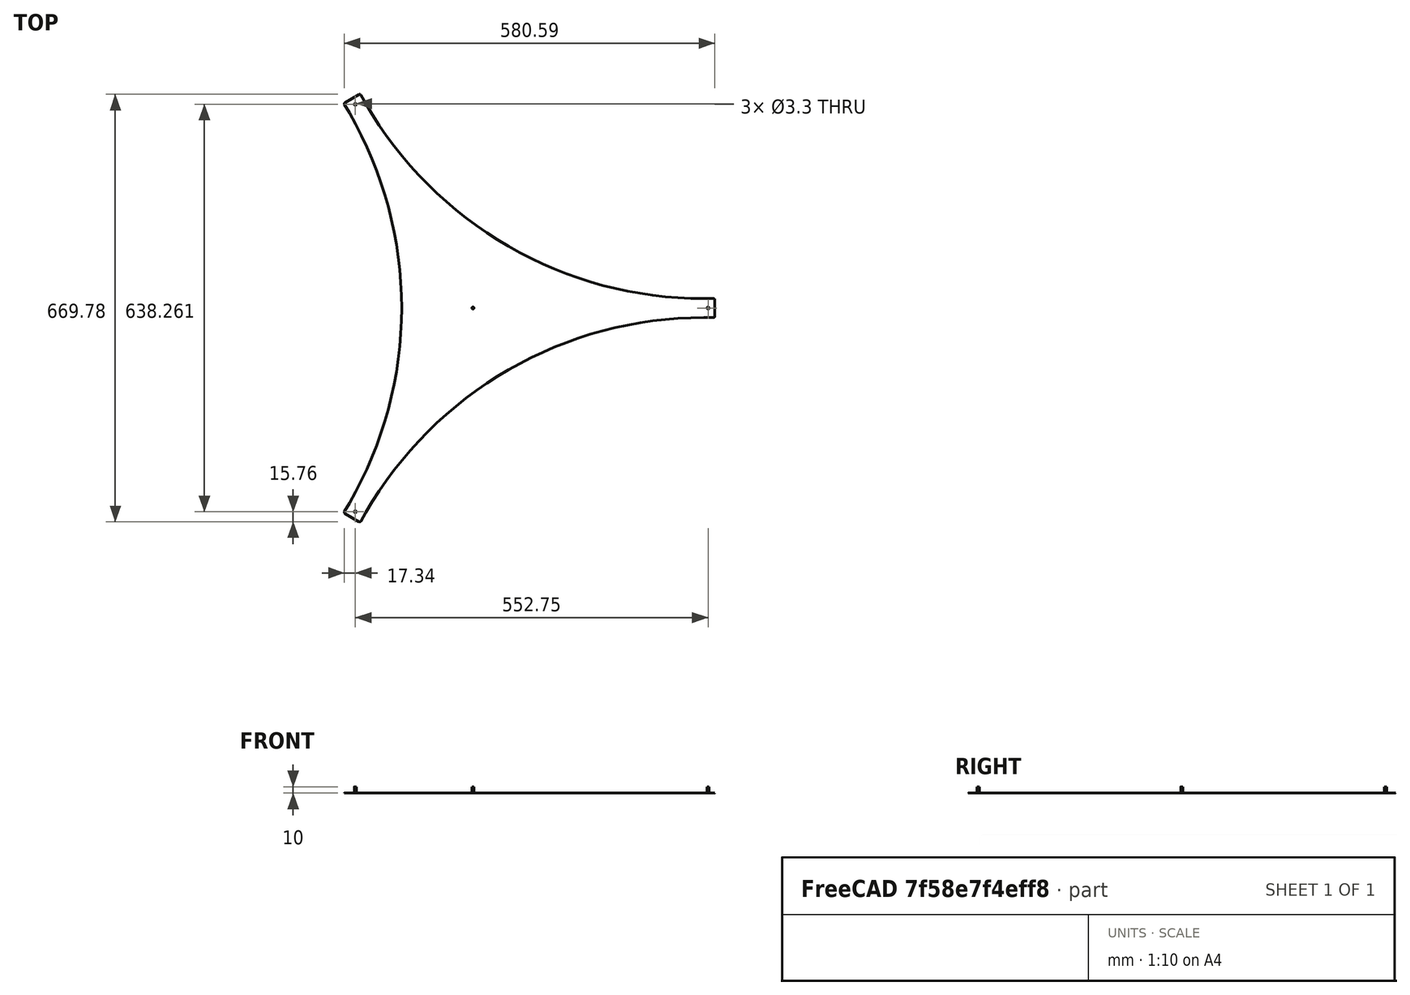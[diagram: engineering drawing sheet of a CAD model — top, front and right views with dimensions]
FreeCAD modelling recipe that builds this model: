
FCSTD DOCUMENT  (FreeCAD 1.1R38827 (Git))
Label: composit_stand3_hat_top_model
License: All rights reserved
LicenseURL: http://en.wikipedia.org/wiki/All_rights_reserved
objects: PartDesign::SubShapeBinder×2, Part::FeaturePython×2, PartDesign::FeaturePython×1, Part::Cylinder×1, Part::MultiFuse×1, PartDesign::Boolean×1, PartDesign::CoordinateSystem×1, PartDesign::Body×1
note: 12 computed .brp shape members not serialized (recipe doc carries the construction recipe); baked Part::Feature solids carry a one-line shape summary decoded from their .brp
EXTERNAL_REF file=composit_stand3_hat_top_main.FCStd obj=Connect
EXTERNAL_REF file=composit_stand3_basement_bottom_main.FCStd obj=Placment

FEATURE [PartDesign::SubShapeBinder] Binder
  BindCopyOnChange = 0
  BindMode = 0
  ClaimChildren = true
  Fuse = false
  MakeFace = true
  OffsetFill = false
  OffsetIntersection = false
  OffsetJoinType = 0
  OffsetOpenResult = false
  PartialLoad = false
  Relative = true
  Support = -> [<external composit_stand3_hat_top_main.FCStd>#Connect]
  _Version = 2
FEATURE [PartDesign::SubShapeBinder] Binder001
  BindCopyOnChange = 0
  BindMode = 0
  ClaimChildren = true
  Context = -> Body [Binder001.]
  Fuse = false
  MakeFace = true
  OffsetFill = false
  OffsetIntersection = false
  OffsetJoinType = 0
  OffsetOpenResult = false
  PartialLoad = false
  Relative = true
  Support = -> [Binder]
  _Version = 2
FEATURE [PartDesign::FeaturePython] BaseBend  # WARN: FeaturePython — macro-defined, semantics opaque (R4)
  BendSide = 0
  BendSketch = -> Binder001
  MidPlane = false
  Reverse = false
  Suppressed = false
  length = 100
  radius = 0.3
  thickness = 0.1
FEATURE [Part::Cylinder] Cylinder  label="fix_hole_base"
  Angle = 360
  AttacherType = Attacher::AttachEngine3D
  FirstAngle = 0
  Height = 10
  Radius = 1.65
  SecondAngle = 0
FEATURE [Part::FeaturePython] PolarArray  label="fix_placement"  # WARN: FeaturePython — macro-defined, semantics opaque (R4)
  Alignment = 0
  AttacherType = Attacher::AttachEngine3D
  CellStart = A1
  Count = 3
  DistributionLaw = 0
  EndInclusive = false
  ExposePlacement = false
  FlipX = false
  FlipZ = false
  GeneratorMode = 0
  MarkerShape = 1
  MarkerSize = 0
  NumElements = 3
  OrientMode = 2
  Radius = 368.5
  Reverse = false
  SpanEnd = 360
  SpanStart = 0
  Step = 120
  Type = lattice2PolarArray2.PolarArray
  UseArcRadius = false
  UseArcRange = 0
  VSGVersion = 1
  Values = 0.0 | 120.0 | 240.0
  ValuesSource = 2
  isLattice = 1
  expr: Radius = <<composit_stand3_basement_bottom_main>>#<<bar_placement>>.Placement.Base.x - 15 mm
FEATURE [Part::FeaturePython] Populate  label="Populate fix_placement with fix_hole_base"  # WARN: FeaturePython — macro-defined, semantics opaque (R4)
  Copying = 0
  ExposePlacement = false
  MarkerShape = 1
  MarkerSize = 0
  NumElements = 0
  Object = -> Cylinder
  OutputCompounding = 1
  PlacementsTo = -> PolarArray
  Referencing = 0
  Type = lattice2PopulateCopies.LatticePopulateCopies
  isLattice = 0
FEATURE [Part::MultiFuse] Fusion
  Shapes = -> [Populate]
FEATURE [PartDesign::Boolean] Boolean
  BaseFeature = -> BaseBend
  Group = -> [Fusion]
  Suppressed = false
  Type = 1
  UsePlacement = true
FEATURE [PartDesign::CoordinateSystem] Local_CS  label="base_LCS"
  AttacherType = Attacher::AttachEngine3D
  AttachmentSupport = -> [XY_Plane]
  MapMode = 5
FEATURE [PartDesign::Body] Body  label="hat_top"
  AllowCompound = false
  Group = -> [Binder001,BaseBend,Boolean,Local_CS]
  Origin = -> Origin
  Tip = -> Boolean
